# Revit family: CBCGTYP016
name_source: partatom
category: Furniture
units: mm (PartAtom-declared; Revit-internal decimal feet)

## family parameters
Always vertical = Yes
Cut with Voids When Loaded = No
OmniClass Number = 23.40.20.00
OmniClass Title = General Furniture and Specialties
Render Appearance Source = Family Geometry
Room Calculation Point = No
Shared = No
Work Plane-Based = No

## types (1)
- CBCGTYP016
    Cost = 21228 $
    Default Elevation = 0 mm  [stored 0 ft]
    Description = 1 x Table Desk, Rectangular, 2mm, O-Leg, 30Dx60Wx29H, 1 x CBX Cntlvr Hat 24x60W/ W/Pwr W/Access, 2 x Cbx 2d Full Depth Lat 24dx28hx36w, 2 x CBX Wall Mounted L Shelf Vertical 52Hx36Wx12D, 2 x Cbx Tackboard Wall Mount 53hx30w
    Exported From CET Designer = Yes
    Manufacturer = AIS
    Model = T-RCR306029OLG
    Show CBCGTYP016 = Yes
    VisibilityIndex = 0

note: [stored X ft] marks values corroborated as IEEE doubles in the binary element streams (Revit-internal decimal feet)

## geometry (parser evidence)
native form markers: Sweep x3
no freeform markers — native parametric forms only
